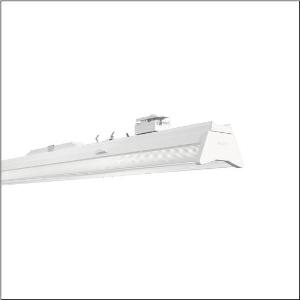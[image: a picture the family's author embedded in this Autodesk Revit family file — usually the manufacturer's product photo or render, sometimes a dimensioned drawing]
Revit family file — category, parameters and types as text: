
# Revit family: licross_r__11_performance_mo_51td16dn445g_6250
name_source: partatom
category: Lighting Fixtures
units: mm (PartAtom-declared; Revit-internal decimal feet)

## family parameters
Cut with Voids When Loaded = No
Host = Face
Light Source = No
Part Type = Normal
Room Calculation Point = No
Round Connector Dimension = Use Diameter
Shared = No

## types (1)
- --- (1 x LED, 4520 lm, 24.3 W, 4000K)
    Apparent Load = 24 VA
    CIE Flux Codes = 66 88 96 79 100
    Color Rendering = 80
    Color Temperature = 4000K
    Default Elevation = 1800 mm
    Description = Licross® 11 Performance MO, luminaire insert, of sheet steel, galvanised, coil coated, white, length: 1.500mm, width: 120mm, height: 123mm, LED rated luminous flux: 4.520lm, light colour: 840, control gear: DALI 2, with plug, 5-pole, with phase selection, mains connection: 220..240V, AC, 50/60Hz, rated input power: 24W, halogen-free wiring, primary light control with lens, of plastic, primary optical cover: cover, of PMMA, CAT 2 (L<= 3000cd/m²), light emission: direct/indirect distribution, primary light characteristic: symmetric, protection rating (complete): IP54, insulation class (complete): insulation class I (protective earthing), certification: CE, ENEC, VDE, UKCA, protection symbol: D if used in an environment with non-conductive dust loads with corresponding accessories, impact resistance: IK06, permissible ambient temperature for indoor applications: -25..+45°C, corresponds to IFS (International Featured Standards) requirements for safety and quality in the food industry, reducing of maximum allowable ambient temperature of 5°C with ceiling mounting, LABS conformity tested according to VDMA 24364:2018-05, packaging unit: 1 piece
    Height = 114 mm
    Lamp = 1 x LED
    Lamp Light Flux = 4520 lm
    Lamp Power = 24.3 W
    Lamp count = 1
    Length = 1500 mm
    Luminous efficacy = 186 lm/W
    Manufacturer = Siteco
    ModVariant = No
    Model = 51TD16DN445G
    Mounting Place = Ceiling
    Mounting Type = Pendant
    Number of Poles = 1
    OnlyDefault = Yes
    Power Factor = 1
    Product Name = Licross® 11 Performance MO
    Product group = luminaire insert
    ProductGroupID = 901
    Protection Class = Protection class I
    Protection Degree = IP 54
    RLX_Detail_Level = 1
    RLX_Emergency_Light_Flux = 0 lm
    RLX_Emergency_Type = 0
    RLX_Emergency_Type_DB = No
    RlxData = <blob elided: 33769 chars, md5=1ff7d74c>
    Socket = socket
    Standby Power = 0 W
    System Light Flux = 4520 lm
    System Power = 24 W
    Type Comments = factory setting: luminous flux: 100 % | dim-lin: 254 | 161 mA
    Type Image = l_1256138.jpg
    URL = http://relux.com
    VarID = @adj_004953
    Voltage = 0 V
    Weight = 0.00 kg
    Width = 120 mm

## geometry (parser evidence)
native form markers: Blend x4, Sweep x14
no freeform markers — native parametric forms only
